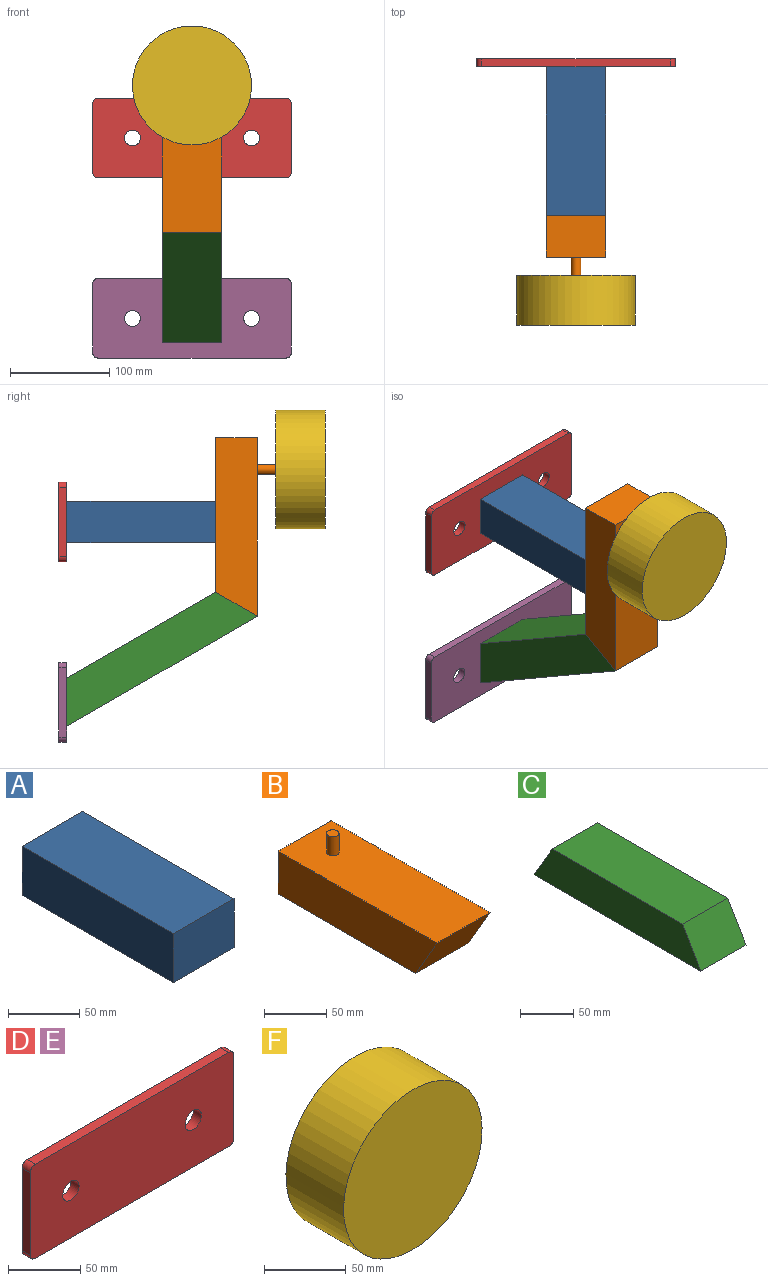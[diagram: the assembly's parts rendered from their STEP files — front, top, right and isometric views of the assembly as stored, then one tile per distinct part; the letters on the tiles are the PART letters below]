
ASSEMBLY  parts=6 mates=4
PART A: 6 faces, bbox 60x150x42 mm
  f0: plane 150x42mm, normal (-1,0,0), area 6300mm2, adj f1,f3,f4,f5
  f1: plane 150x60mm, normal (0,0,-1), area 9000mm2, adj f0,f2,f4,f5
  f2: plane 150x42mm, normal (1,0,0), area 6300mm2, adj f1,f3,f4,f5
  f3: plane 150x60mm, normal (0,0,1), area 9000mm2, adj f0,f2,f4,f5
  f4: plane 60x42mm, normal (0,-1,0), area 2520mm2, adj f0,f1,f2,f3
  f5: plane 60x42mm, normal (0,1,0), area 2520mm2, adj f0,f1,f2,f3
PART B: 8 faces, bbox 60x180x60.5 mm
  f0: cylinder r=5mm len=18.5mm, axis (0,0,-1), area 581.2mm2, adj f1,f5
  f1: plane 10x10mm, normal (0,0,1), area 78.5mm2, adj f0
  f2: plane 155.75x60mm, normal (0,0,-1), area 9345.1mm2, adj f3,f4,f6,f7
  f3: plane 180x42mm, normal (-1,0,0), area 7050.8mm2, adj f2,f5,f6,f7
  f4: plane 180x42mm, normal (1,0,0), area 7050.8mm2, adj f2,f5,f6,f7
  f5: plane 180x60mm, normal (0,0,1), area 10721.5mm2, adj f0,f3,f4,f6,f7
  f6: plane 60x42mm, normal (0,1,0), area 2520mm2, adj f2,f3,f4,f5
  f7: plane 60x42mm, normal (0,-0.87,-0.5), area 2909.8mm2, adj f2,f3,f4,f5
PART C: 6 faces, bbox 60x222x42 mm
  f0: plane 222x42mm, normal (-1,0,0), area 8305.6mm2, adj f2,f3,f4,f5
  f1: plane 222x42mm, normal (1,0,0), area 8305.6mm2, adj f2,f3,f4,f5
  f2: plane 222x60mm, normal (0,0,-1), area 13320mm2, adj f0,f1,f4,f5
  f3: plane 173.5x60mm, normal (0,0,1), area 10410.2mm2, adj f0,f1,f4,f5
  f4: plane 60x42mm, normal (0,0.87,0.5), area 2909.8mm2, adj f0,f1,f2,f3
  f5: plane 60x42mm, normal (0,-0.87,0.5), area 2909.8mm2, adj f0,f1,f2,f3
PART D: 12 faces, bbox 200x8x80 mm
  f0: plane 190x8mm, normal (0,0,1), area 1520mm2, adj f4,f5,f6,f9
  f1: plane 70x8mm, normal (-1,0,0), area 560mm2, adj f4,f5,f6,f7
  f2: plane 190x8mm, normal (0,0,-1), area 1520mm2, adj f4,f5,f7,f8
  f3: plane 70x8mm, normal (1,0,0), area 560mm2, adj f4,f5,f8,f9
  f4: plane 200x80mm, normal (0,-1,0), area 15576.4mm2, adj f0,f1,f2,f3,f6,f7,f8,f9
  f5: plane 200x80mm, normal (0,1,0), area 15576.4mm2, adj f0,f1,f2,f3,f6,f7,f8,f9
  f6: cylinder r=5mm len=8mm, axis (0,-1,0), area 62.8mm2, adj f0,f1,f4,f5
  f7: cylinder r=5mm len=8mm, axis (0,1,0), area 62.8mm2, adj f1,f2,f4,f5
  f8: cylinder r=5mm len=8mm, axis (0,-1,0), area 62.8mm2, adj f2,f3,f4,f5
  f9: cylinder r=5mm len=8mm, axis (0,1,0), area 62.8mm2, adj f0,f3,f4,f5
  f10: cylinder r=8mm len=16mm, axis (0,-1,0), area 402.1mm2, adj f4,f5
  f11: cylinder r=8mm len=16mm, axis (0,-1,0), area 402.1mm2, adj f4,f5
PART E: same geometry as D
PART F: 3 faces, bbox 120x50x120 mm
  f0: cylinder r=60mm len=120mm, axis (0,1,0), area 18849.6mm2, adj f1,f2
  f1: plane 120x120mm, normal (0,-1,0), area 11309.7mm2, adj f0
  f2: plane 120x120mm, normal (0,1,0), area 11309.7mm2, adj f0
PLACE A t=(-30,210.5,-74)mm
PLACE B rot(axis=(1,0,0),90deg) t=(-30,60.5,32)mm
PLACE C rot(axis=(-1,0,0),30deg) t=(-30,210.76,-259)mm
PLACE D t=(0,218.5,-53)mm
PLACE E t=(0,218.76,-234.75)mm
PLACE F at identity
MATE fastened E.f4 <-> C.f4  axis (0,-1,0) through (0,210.76,-234.75)mm
MATE fastened C.f5 <-> B.f7  axis (0,-0.5,0.87) through (0,39.5,-135.88)mm
MATE fastened A.f4 <-> B.f2  axis (0,-1,0) through (0,60.5,-53)mm
MATE fastened D.f4 <-> A.f5  axis (0,-1,0) through (0,210.5,-53)mm
